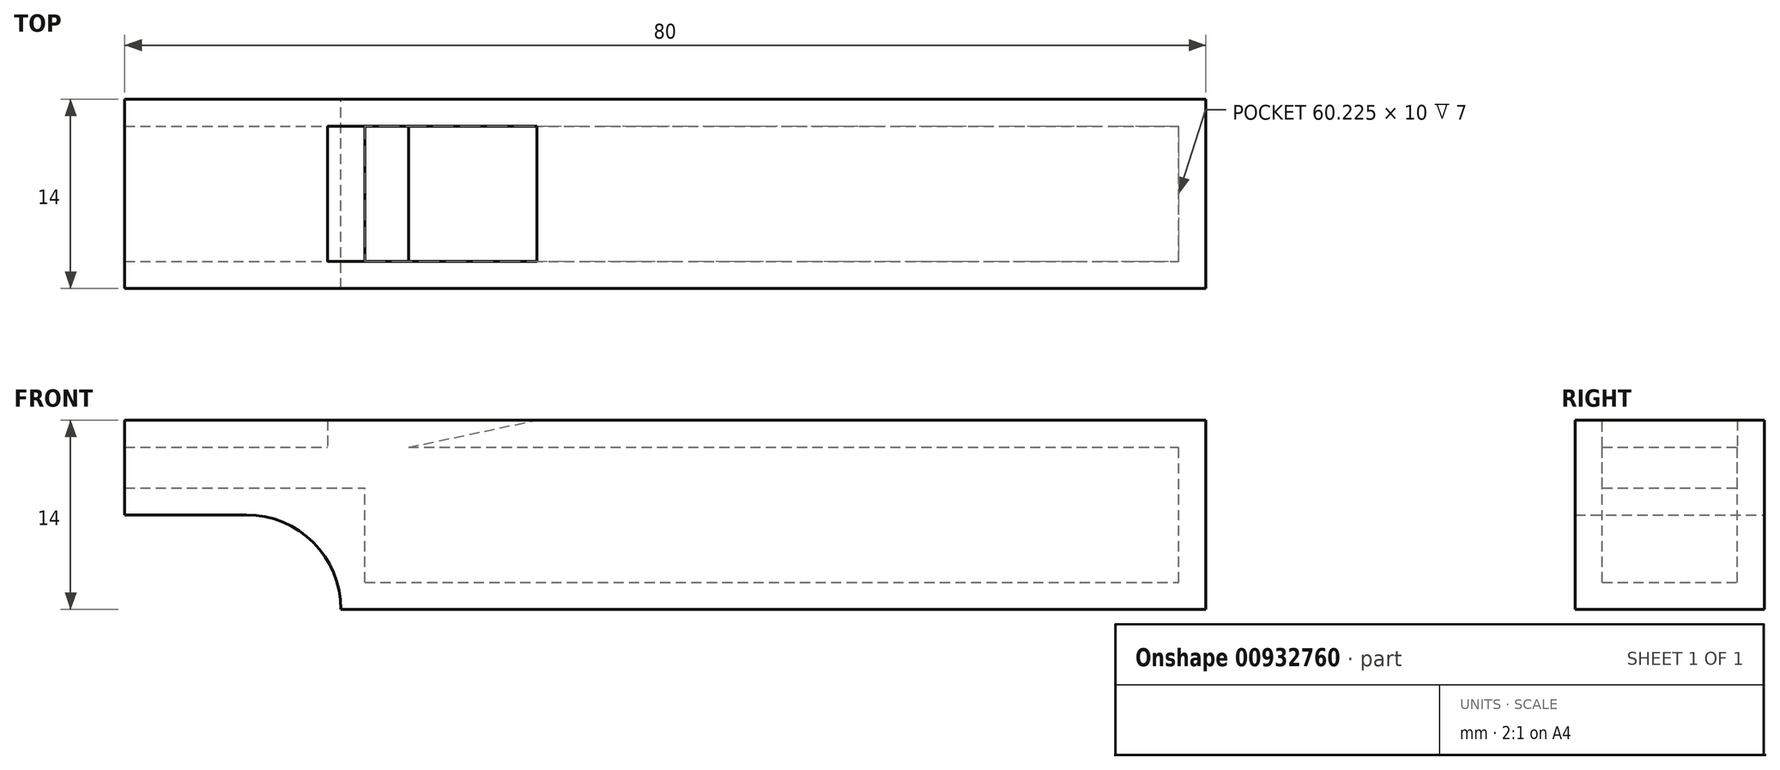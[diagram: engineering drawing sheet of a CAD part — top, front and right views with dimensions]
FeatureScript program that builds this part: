
annotation { "Feature Type Name" : "Feature", "Feature Type Description" : "" }
export const myFeature = defineFeature(function(context is Context, id is Id, definition is map)
    precondition{}
    {
        {
            var Q0;
            Q0=qCreatedBy(makeId("Front.planeOp"),FACE);
            var sketch = newSketch(context, id + "F0", { "sketchPlane" : qUnion([Q0])});
            skLineSegment(sketch, "E0.bottom", {"start": v(0, 0) * mm, "end": v(80, 0) * mm});
            skLineSegment(sketch, "E0.top", {"start": v(0, 14) * mm, "end": v(80, 14) * mm});
            skLineSegment(sketch, "E0.left", {"start": v(0, 0) * mm, "end": v(0, 14) * mm});
            skLineSegment(sketch, "E0.right", {"start": v(80, 0) * mm, "end": v(80, 14) * mm});
            skLineSegment(sketch, "E1.bottom", {"start": v(0, 0) * mm, "end": v(9, 0) * mm});
            skLineSegment(sketch, "E1.top", {"start": v(0, 7) * mm, "end": v(9, 7) * mm});
            skLineSegment(sketch, "E1.left", {"start": v(0, 0) * mm, "end": v(0, 7) * mm});
            skLineSegment(sketch, "E1.right", {"start": v(9, 0) * mm, "end": v(9, 7) * mm});
            skCircle(sketch, "E2", {"center": v(9, 0) * mm, "radius": 7 * mm});
            skSolve(sketch);
        }
        {
            var Q0;
            Q0=makeQuery(id+"F0.imprint","IMPRINT",FACE,{"disambiguationData":[TD([[makeQuery(id+"F0.imprint","IMPRINT",EDGE,{"derivedFrom":sQuery(id+"F0.wireOp",EDGE,"E0.top")}),-1.0]])]});
            extrude(context, id + "F1", {"entities" : qUnion([Q0]), "depth" : 2 * mm, "offsetDistance" : 25 * mm});
        }
        {
            var Q0;
            Q0=makeQuery(id+"F1.opExtrude","CAP_FACE",FACE,{"disambiguationData":[OSD([sQuery(id+"F0.wireOp",EDGE,"E0.bottom"),sQuery(id+"F0.wireOp",EDGE,"E0.top"),sQuery(id+"F0.wireOp",EDGE,"E0.left"),sQuery(id+"F0.wireOp",EDGE,"E0.right"),sQuery(id+"F0.wireOp",EDGE,"E1.top"),sQuery(id+"F0.wireOp",EDGE,"E2")])],"isStart":false});
            var sketch = newSketch(context, id + "F2", { "sketchPlane" : qUnion([Q0])});
            skLineSegment(sketch, "E3.0", {"start": v(0, 9) * mm, "end": v(17.77, 9) * mm});
            skLineSegment(sketch, "E3.1", {"start": v(0, 12) * mm, "end": v(15, 12) * mm});
            skLineSegment(sketch, "E3.2", {"start": v(78, 2) * mm, "end": v(78, 12) * mm});
            skLineSegment(sketch, "E3.3", {"start": v(17.77, 2) * mm, "end": v(78, 2) * mm});
            skLineSegment(sketch, "E4", {"start": v(17.77, 2) * mm, "end": v(17.77, 9) * mm});
            skLineSegment(sketch, "E5", {"start": v(15, 14) * mm, "end": v(15, 12) * mm});
            skLineSegment(sketch, "E6", {"start": v(21, 12) * mm, "end": v(30.5, 14) * mm});
            skLineSegment(sketch, "E7.trimOffspring", {"start": v(21, 12) * mm, "end": v(78, 12) * mm});
            skSolve(sketch);
        }
        {
            var Q0;
            {var subQ3=sQuery(id+"F2.wireOp",EDGE,"E3.0");Q0=makeQuery(id+"F2.imprint","IMPRINT",FACE,{"disambiguationData":[TD([[makeQuery(id+"F2.imprint","IMPRINT",EDGE,{"derivedFrom":subQ3}),-1.0]])]});}
            var Q1;
            {var subQ0=sQuery(id+"F2.wireOp",EDGE,"E3.1");Q1=makeQuery(id+"F2.imprint","IMPRINT",FACE,{"disambiguationData":[TD([[makeQuery(id+"F2.imprint","IMPRINT",EDGE,{"derivedFrom":subQ0}),1.0]])]});}
            extrude(context, id + "F3", {"entities" : qUnion([Q0, Q1]), "operationType" : NewBodyOperationType.ADD, "depth" : 5 * mm, "offsetDistance" : 25 * mm});
        }
        {
            var Q0;
            Q0=makeQuery(id+"F1.opExtrude","SWEPT_BODY",BODY,{"disambiguationData":[OSD([sQuery(id+"F0.wireOp",EDGE,"E0.bottom"),sQuery(id+"F0.wireOp",EDGE,"E0.top"),sQuery(id+"F0.wireOp",EDGE,"E0.left"),sQuery(id+"F0.wireOp",EDGE,"E0.right"),sQuery(id+"F0.wireOp",EDGE,"E1.top"),sQuery(id+"F0.wireOp",EDGE,"E2")])]});
            var Q1;
            Q1=makeQuery(id+"F3.opExtrude","CAP_FACE",FACE,{"disambiguationData":[OSD([sQuery(id+"F0.wireOp",EDGE,"E0.bottom"),sQuery(id+"F0.wireOp",EDGE,"E0.top"),sQuery(id+"F0.wireOp",EDGE,"E0.left"),sQuery(id+"F0.wireOp",EDGE,"E0.right"),sQuery(id+"F0.wireOp",EDGE,"E1.top"),sQuery(id+"F0.wireOp",EDGE,"E2"),sQuery(id+"F2.wireOp",EDGE,"E3.0"),sQuery(id+"F2.wireOp",EDGE,"E3.2"),sQuery(id+"F2.wireOp",EDGE,"E3.3"),sQuery(id+"F2.wireOp",EDGE,"E4"),sQuery(id+"F2.wireOp",EDGE,"E6"),sQuery(id+"F2.wireOp",EDGE,"E7.trimOffspring")])],"isStart":false});
            mirror(context, id + "F4", {"operationType" : NewBodyOperationType.ADD, "entities" : qUnion([Q0]), "mirrorPlane" : qUnion([Q1])});
        }
    });
